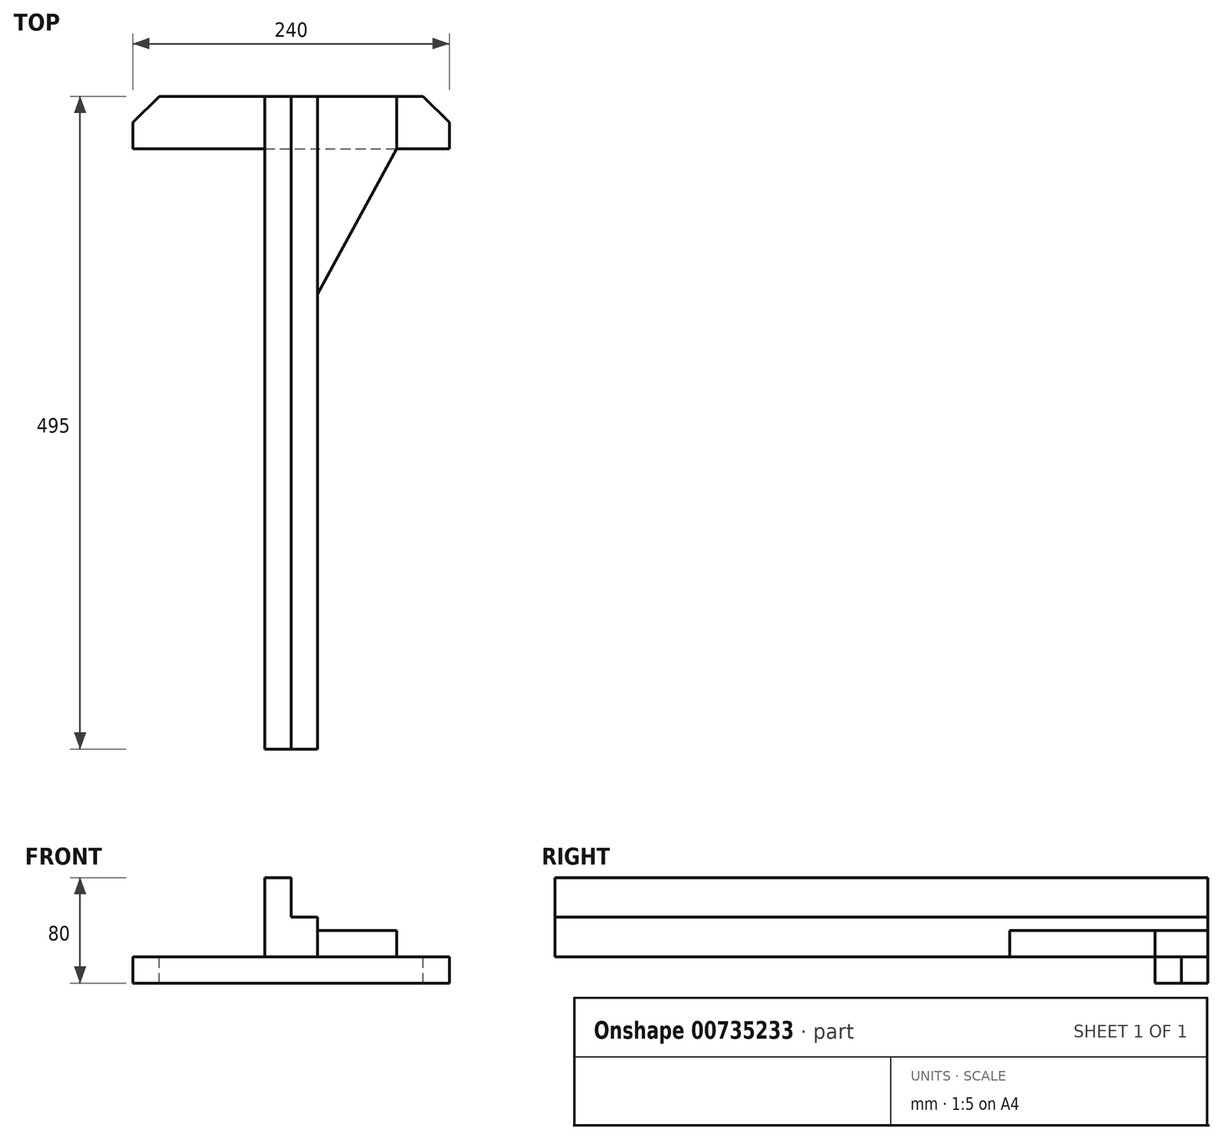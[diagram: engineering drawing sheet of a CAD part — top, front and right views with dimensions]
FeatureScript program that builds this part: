
annotation { "Feature Type Name" : "Feature", "Feature Type Description" : "" }
export const myFeature = defineFeature(function(context is Context, id is Id, definition is map)
    precondition{}
    {
        {
            var Q0;
            Q0=qCreatedBy(makeId("Top.planeOp"),FACE);
            var sketch = newSketch(context, id + "F0", { "sketchPlane" : qUnion([Q0])});
            skLineSegment(sketch, "E0.bottom", {"start": v(20, 40) * mm, "end": v(120, 40) * mm});
            skLineSegment(sketch, "E0.top", {"start": v(0, 0) * mm, "end": v(120, 0) * mm});
            skLineSegment(sketch, "E0.left", {"start": v(0, 20) * mm, "end": v(0, 0) * mm});
            skLineSegment(sketch, "E0.right", {"start": v(120, 40) * mm, "end": v(120, 0) * mm});
            skLineSegment(sketch, "E1", {"start": v(20, 40) * mm, "end": v(0, 20) * mm});
            skPoint(sketch, "E2.orphan", {"position": v(0, 40) * mm});
            skLineSegment(sketch, "E3.MirrorCS", {"start": v(220, 40) * mm, "end": v(120, 40) * mm});
            skLineSegment(sketch, "E4.MirrorCS", {"start": v(220, 40) * mm, "end": v(240, 20) * mm});
            skLineSegment(sketch, "E5.MirrorCS", {"start": v(240, 20) * mm, "end": v(240, 0) * mm});
            skLineSegment(sketch, "E6.MirrorCS", {"start": v(240, 0) * mm, "end": v(120, 0) * mm});
            skSolve(sketch);
        }
        {
            var Q0;
            Q0 = qSketchRegion(id + "F0", true);
            extrude(context, id + "F1", {"entities" : qUnion([Q0]), "oppositeDirection" : true, "depth" : 20 * mm, "offsetDistance" : 25 * mm});
        }
        {
            var Q0;
            Q0=qCreatedBy(makeId("Top.planeOp"),FACE);
            var sketch = newSketch(context, id + "F2", { "sketchPlane" : qUnion([Q0])});
            skLineSegment(sketch, "E7.bottom", {"start": v(120, 40) * mm, "end": v(100, 40) * mm});
            skLineSegment(sketch, "E7.top", {"start": v(120, -455) * mm, "end": v(100, -455) * mm});
            skLineSegment(sketch, "E7.left", {"start": v(120, 40) * mm, "end": v(120, -455) * mm});
            skLineSegment(sketch, "E7.right", {"start": v(100, 40) * mm, "end": v(100, -455) * mm});
            skLineSegment(sketch, "E8.MirrorCS", {"start": v(120, 40) * mm, "end": v(140, 40) * mm});
            skLineSegment(sketch, "E9.MirrorCS", {"start": v(140, 40) * mm, "end": v(140, -455) * mm});
            skLineSegment(sketch, "E10.MirrorCS", {"start": v(120, -455) * mm, "end": v(140, -455) * mm});
            skLineSegment(sketch, "E11", {"start": v(140, 40) * mm, "end": v(200, 40) * mm});
            skLineSegment(sketch, "E12", {"start": v(200, 40) * mm, "end": v(200, 0) * mm});
            skLineSegment(sketch, "E13", {"start": v(200, 0) * mm, "end": v(140, -110) * mm});
            skLineSegment(sketch, "E14", {"start": v(140, -110) * mm, "end": v(140, 40) * mm});
            skSolve(sketch);
        }
        {
            var Q0;
            Q0=makeQuery(id+"F2.imprint","IMPRINT",FACE,{"disambiguationData":[TD([[makeQuery(id+"F2.imprint","IMPRINT",EDGE,{"derivedFrom":sQuery(id+"F2.wireOp",EDGE,"E7.bottom")}),1.0]])]});
            extrude(context, id + "F3", {"entities" : qUnion([Q0]), "operationType" : NewBodyOperationType.ADD, "depth" : 60 * mm, "offsetDistance" : 25 * mm});
        }
        {
            var Q0;
            Q0=makeQuery(id+"F2.imprint","IMPRINT",FACE,{"disambiguationData":[TD([[makeQuery(id+"F2.imprint","IMPRINT",EDGE,{"derivedFrom":sQuery(id+"F2.wireOp",EDGE,"E7.left")}),1.0]])]});
            extrude(context, id + "F4", {"entities" : qUnion([Q0]), "operationType" : NewBodyOperationType.ADD, "depth" : 30 * mm, "offsetDistance" : 25 * mm});
        }
        {
            var Q0;
            Q0=makeQuery(id+"F2.imprint","IMPRINT",FACE,{"disambiguationData":[TD([[makeQuery(id+"F2.imprint","IMPRINT",EDGE,{"derivedFrom":sQuery(id+"F2.wireOp",EDGE,"E11")}),-1.0]])]});
            extrude(context, id + "F5", {"entities" : qUnion([Q0]), "operationType" : NewBodyOperationType.ADD, "depth" : 20 * mm, "offsetDistance" : 25 * mm});
        }
    });
